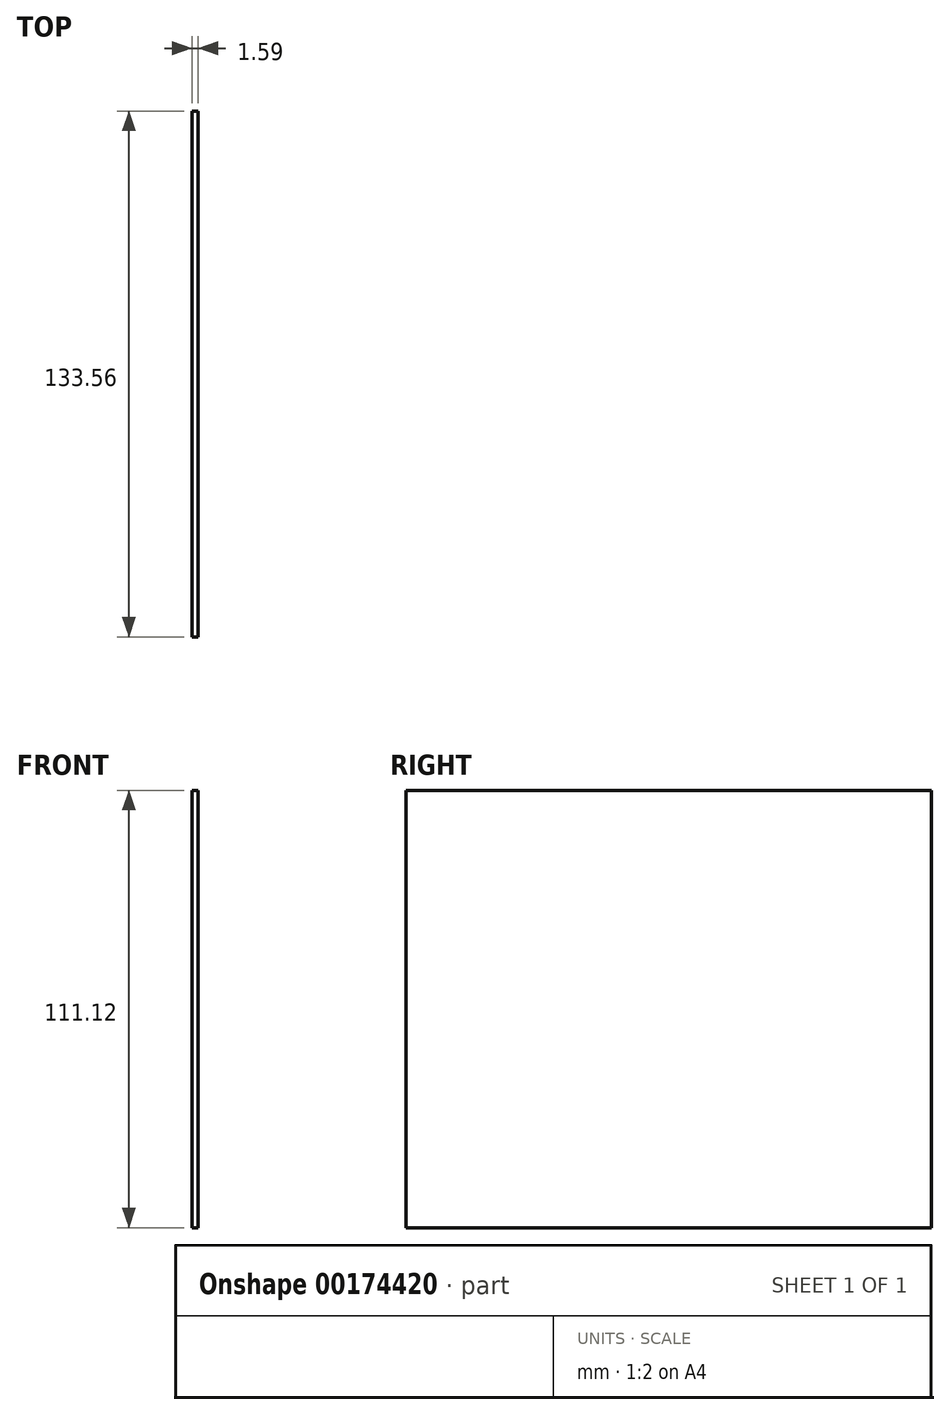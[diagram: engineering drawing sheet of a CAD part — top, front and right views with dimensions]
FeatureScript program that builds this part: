
annotation { "Feature Type Name" : "Feature", "Feature Type Description" : "" }
export const myFeature = defineFeature(function(context is Context, id is Id, definition is map)
    precondition{}
    {
        {
            var Q0;
            Q0=qCreatedBy(makeId("Right.planeOp"),FACE);
            var sketch = newSketch(context, id + "F0", { "sketchPlane" : qUnion([Q0])});
            skLineSegment(sketch, "E0.bottom", {"start": v(66.78, 55.56) * mm, "end": v(-66.78, 55.56) * mm});
            skLineSegment(sketch, "E0.top", {"start": v(66.78, -55.56) * mm, "end": v(-66.78, -55.56) * mm});
            skLineSegment(sketch, "E0.left", {"start": v(66.78, 55.56) * mm, "end": v(66.78, -55.56) * mm});
            skLineSegment(sketch, "E0.right", {"start": v(-66.78, 55.56) * mm, "end": v(-66.78, -55.56) * mm});
            skPoint(sketch, "E0.middle", {"position": v(0, 0) * mm});
            skSolve(sketch);
        }
        {
            var Q0;
            Q0 = qSketchRegion(id + "F0", true);
            extrude(context, id + "F1", {"entities" : qUnion([Q0]), "depth" : 1.59 * mm});
        }
    });
